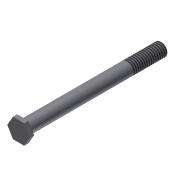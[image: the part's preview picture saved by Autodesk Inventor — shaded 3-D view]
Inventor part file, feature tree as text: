
AUTODESK INVENTOR PART (.ipt)
format: ipt  version: 2011 (Build 150239000, 239)  size: 89,088 bytes
history: native  units: in
note: dims shown in document units (in); Inventor stores cm internally (conversion verified against a paired STEP export)
features: extrude x2, sketch x2, thread x1, chamfer x1
ambient origin geometry x8: Origin, YZ Plane, XZ Plane, XY Plane, X Axis, Y Axis, Z Axis, Center Point
bodies: Solid1 (feature_tree)
feature tree (6):
  extrude  "Extrusion1"  Depth=4.0in TaperAngle=0.0deg
  extrude  "Extrusion2"  Depth=0.125in TaperAngle=0.0deg
  thread  "Thread1"  [1 undecoded]
  chamfer  "Chamfer1"  Distance=0.02in Angle=45.0deg
  sketch  "Sketch1"  dims[d0=0.375in d1=4.0in d2=0.0in]
  sketch  "Sketch2"  dims[d3=0.5625in d4=0.125in d5=0.0in d6=1.0in d7=0.0in d8=0.02in d9=0.125in d10=45.0deg]
note: 1 required parameter value undecoded (feature->parameter linkage not recoverable at this tier; creation-order binding heuristic only, values carry confidence <= 0.55)
